# Revit family: Heat_pump_MasterTherm_BA45IP
name_source: partatom
category: Mechanické zařízení
units: mm (PartAtom-declared; Revit-internal decimal feet)

## family parameters
Bod výpočtu místnosti = Ne
Klasifikace = Žádné
Kóta kulaté spojky = Použít průměr
Nadpis OmniClass = Climate Control (HVAC)
Ořezat dutým tvarem při načtení = Ne
Sdílené = Ne
Typ dílu = Normální
Vždy vertikální = Ano
Založené na pracovní rovině = Ne
Číslo OmniClass = 23.75.00.00

## types (1)
- Heat_pump_MasterTherm_BA45IP
    Condesate = 40 mm  [stored 0.131234 ft]
    El. bushings 2xPG21 = 1
    El. bushings 2xPG29 = 1
    Hot water inlet = 25 mm  [stored 0.082021 ft]
    Hot water outlet = 25 mm  [stored 0.082021 ft]
    Model = BA45IP
    Popis = Inverter, speed 15 -90 rps; heating capacity 8-25 kW (A7W35); voltage 3x400V; Max. current 25 (32) A; weight 185 kg; W/B overpressure 0,25 MPa; Ref. overpressure 2,9 MPa; air Min/Max -20/+35 °C; water Min/Max 20/65 °C; refrigerant R290
    Voltage = 400 V
    Výchozí výška = 0 mm  [stored 0 ft]
    Výrobce = MasterTherm

note: [stored X ft] marks values corroborated as IEEE doubles in the binary element streams (Revit-internal decimal feet)

## geometry (parser evidence)
native form markers: Sweep x3
no freeform markers — native parametric forms only
